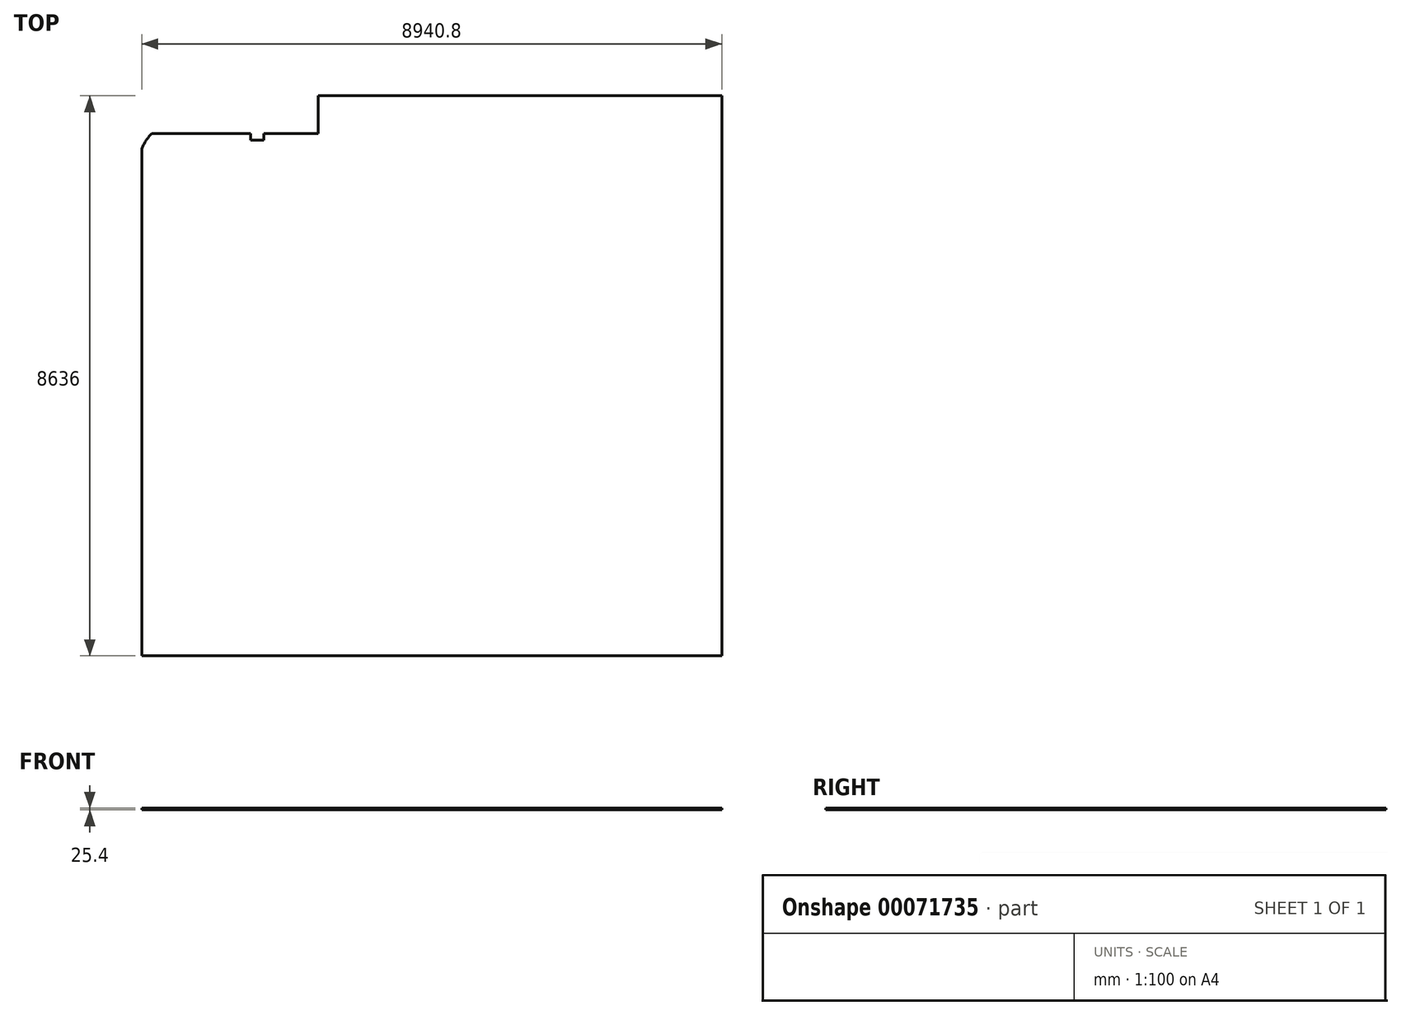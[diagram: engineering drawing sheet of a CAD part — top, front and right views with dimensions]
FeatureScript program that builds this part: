
annotation { "Feature Type Name" : "Feature", "Feature Type Description" : "" }
export const myFeature = defineFeature(function(context is Context, id is Id, definition is map)
    precondition{}
    {
        {
            var Q0;
            Q0=qCreatedBy(makeId("Top.planeOp"),FACE);
            var sketch = newSketch(context, id + "F0", { "sketchPlane" : qUnion([Q0])});
            skLineSegment(sketch, "E0", {"start": v(4934.2, 6012.18) * mm, "end": v(-1288.8, 6012.18) * mm});
            skLineSegment(sketch, "E1", {"start": v(-1288.8, 6012.18) * mm, "end": v(-1288.8, 5427.98) * mm});
            skLineSegment(sketch, "E2", {"start": v(-1288.8, 5427.98) * mm, "end": v(-2127, 5427.98) * mm});
            skLineSegment(sketch, "E3", {"start": v(-4006.6, -2623.82) * mm, "end": v(4934.2, -2623.82) * mm});
            skLineSegment(sketch, "E4", {"start": v(4934.2, 6012.18) * mm, "end": v(4934.2, -2623.82) * mm});
            skLineSegment(sketch, "E5", {"start": v(-2127, 5427.98) * mm, "end": v(-2127, 5326.38) * mm});
            skLineSegment(sketch, "E6", {"start": v(-2127, 5326.38) * mm, "end": v(-2330.2, 5326.38) * mm});
            skLineSegment(sketch, "E7", {"start": v(-2330.2, 5326.38) * mm, "end": v(-2330.2, 5427.98) * mm});
            skLineSegment(sketch, "E8", {"start": v(-2330.2, 5427.98) * mm, "end": v(-4006.6, 5427.98) * mm});
            skLineSegment(sketch, "E9", {"start": v(-4006.6, 5427.98) * mm, "end": v(-4006.6, -2623.82) * mm});
            skCircle(sketch, "E10", {"center": v(4180.05, 5218.03) * mm, "radius": 685.23 * mm});
            skCircle(sketch, "E11", {"center": v(2675.5, -2356.6) * mm, "radius": 724.27 * mm});
            skCircle(sketch, "E12", {"center": v(-3342.7, 4924.03) * mm, "radius": 716.86 * mm});
            skCircle(sketch, "E13", {"center": v(1165.5, -2289.85) * mm, "radius": 702.7 * mm});
            skSolve(sketch);
        }
        {
            var Q0;
            Q0=sQuery(id+"F0.wireOp",EDGE,"E12");
            var Q1;
            Q1=sQuery(id+"F0.wireOp",EDGE,"E10");
            var Q2;
            Q2=sQuery(id+"F0.wireOp",EDGE,"E11");
            var Q3;
            Q3=sQuery(id+"F0.wireOp",EDGE,"E13");
            extrude(context, id + "F1", {"bodyType" : ToolBodyType.SURFACE, "surfaceEntities" : qUnion([Q0, Q1, Q2, Q3]), "depth" : 12.7 * mm});
        }
        {
            var Q0;
            Q0=makeQuery(id+"F0.imprint","IMPRINT",FACE,{"disambiguationData":[TD([[makeQuery(id+"F0.imprint","IMPRINT",EDGE,{"derivedFrom":sQuery(id+"F0.wireOp",EDGE,"E0")}),1.0]])]});
            var Q1;
            {var subQ0=sQuery(id+"F0.wireOp",EDGE,"E12");var subQ1=sQuery(id+"F0.wireOp",EDGE,"E8");var subQ2=makeQuery(id+"F0.imprint","INTERSECT",VERTEX,{"disambiguationData":[OD(0.0)],"derivedFrom":[subQ1,subQ0]});Q1=makeQuery(id+"F0.imprint","IMPRINT",FACE,{"disambiguationData":[TD([[makeQuery(id+"F0.imprint","IMPRINT",EDGE,{"disambiguationData":[TD([[subQ2,-1.0]])],"derivedFrom":subQ1}),1.0]])]});}
            var Q2;
            Q2=makeQuery(id+"F0.imprint","IMPRINT",FACE,{"disambiguationData":[TD([[makeQuery(id+"F0.imprint","IMPRINT",EDGE,{"derivedFrom":sQuery(id+"F0.wireOp",EDGE,"E10")}),1.0]])]});
            var Q3;
            {var subQ0=sQuery(id+"F0.wireOp",EDGE,"E11");var subQ1=sQuery(id+"F0.wireOp",EDGE,"E3");var subQ2=makeQuery(id+"F0.imprint","INTERSECT",VERTEX,{"disambiguationData":[OD(0.0)],"derivedFrom":[subQ1,subQ0]});Q3=makeQuery(id+"F0.imprint","IMPRINT",FACE,{"disambiguationData":[TD([[makeQuery(id+"F0.imprint","IMPRINT",EDGE,{"disambiguationData":[TD([[subQ2,-1.0]])],"derivedFrom":subQ1}),1.0]])]});}
            var Q4;
            {var subQ0=sQuery(id+"F0.wireOp",EDGE,"E13");var subQ1=sQuery(id+"F0.wireOp",EDGE,"E3");var subQ2=makeQuery(id+"F0.imprint","INTERSECT",VERTEX,{"disambiguationData":[OD(0.0)],"derivedFrom":[subQ1,subQ0]});Q4=makeQuery(id+"F0.imprint","IMPRINT",FACE,{"disambiguationData":[TD([[makeQuery(id+"F0.imprint","IMPRINT",EDGE,{"disambiguationData":[TD([[subQ2,-1.0]])],"derivedFrom":subQ1}),1.0]])]});}
            extrude(context, id + "F2", {"entities" : qUnion([Q0, Q1, Q2, Q3, Q4]), "depth" : 25.4 * mm});
        }
    });
